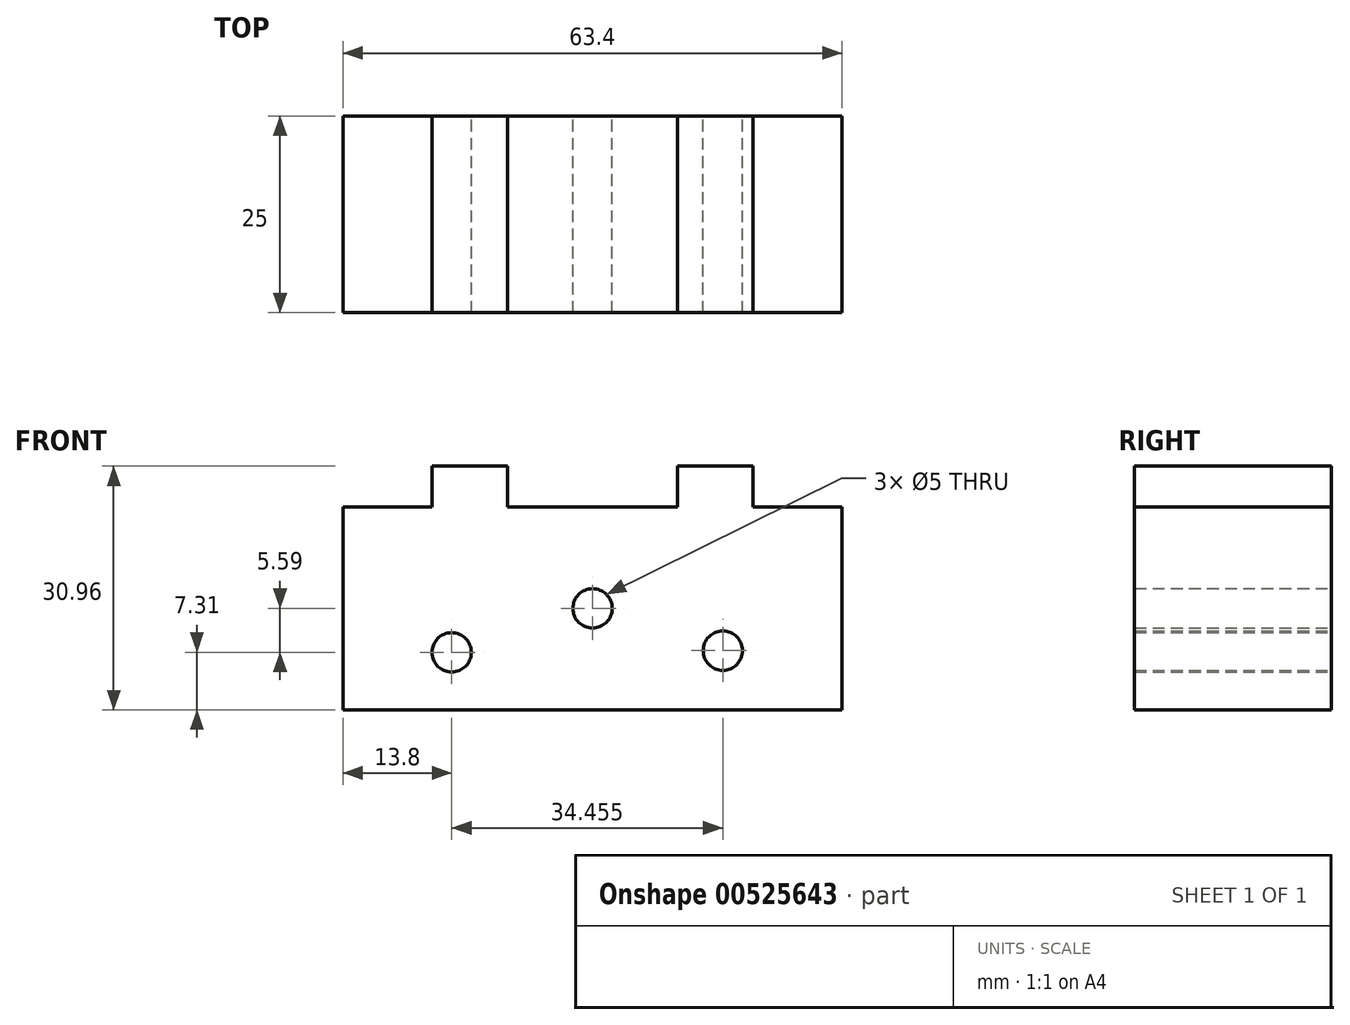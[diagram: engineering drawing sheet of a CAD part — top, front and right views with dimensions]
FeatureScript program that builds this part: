
annotation { "Feature Type Name" : "Feature", "Feature Type Description" : "" }
export const myFeature = defineFeature(function(context is Context, id is Id, definition is map)
    precondition{}
    {
        {
            var Q0;
            Q0=qCreatedBy(makeId("Front.planeOp"),FACE);
            var sketch = newSketch(context, id + "F0", { "sketchPlane" : qUnion([Q0])});
            skLineSegment(sketch, "E0.bottom", {"start": v(-31.7, -12.9) * mm, "end": v(31.7, -12.9) * mm});
            skLineSegment(sketch, "E0.top", {"start": v(-31.7, 12.9) * mm, "end": v(31.7, 12.9) * mm});
            skLineSegment(sketch, "E0.left", {"start": v(-31.7, -12.9) * mm, "end": v(-31.7, 12.9) * mm});
            skLineSegment(sketch, "E0.right", {"start": v(31.7, -12.9) * mm, "end": v(31.7, 12.9) * mm});
            skPoint(sketch, "E0.middle", {"position": v(0, 0) * mm});
            skLineSegment(sketch, "E1.bottom", {"start": v(-10.8, 12.9) * mm, "end": v(-20.4, 12.9) * mm});
            skLineSegment(sketch, "E1.top", {"start": v(-10.8, 18.06) * mm, "end": v(-20.4, 18.06) * mm});
            skLineSegment(sketch, "E1.left", {"start": v(-10.8, 12.9) * mm, "end": v(-10.8, 18.06) * mm});
            skLineSegment(sketch, "E1.right", {"start": v(-20.4, 12.9) * mm, "end": v(-20.4, 18.06) * mm});
            skPoint(sketch, "E1.middle", {"position": v(-15.6, 15.48) * mm});
            skLineSegment(sketch, "E2.bottom", {"start": v(10.8, 12.9) * mm, "end": v(20.4, 12.9) * mm});
            skLineSegment(sketch, "E2.top", {"start": v(10.8, 18.06) * mm, "end": v(20.4, 18.06) * mm});
            skLineSegment(sketch, "E2.left", {"start": v(10.8, 12.9) * mm, "end": v(10.8, 18.06) * mm});
            skLineSegment(sketch, "E2.right", {"start": v(20.4, 12.9) * mm, "end": v(20.4, 18.06) * mm});
            skPoint(sketch, "E2.middle", {"position": v(15.6, 15.48) * mm});
            skCircle(sketch, "E3", {"center": v(0, 0) * mm, "radius": 2.5 * mm});
            skCircle(sketch, "E4", {"center": v(-17.9, -5.59) * mm, "radius": 2.5 * mm});
            skCircle(sketch, "E5", {"center": v(16.56, -5.37) * mm, "radius": 2.5 * mm});
            skSolve(sketch);
        }
        {
            var Q0;
            Q0 = qSketchRegion(id + "F0", true);
            extrude(context, id + "F1", {"entities" : qUnion([Q0]), "depth" : 25 * mm, "offsetDistance" : 25 * mm});
        }
    });
